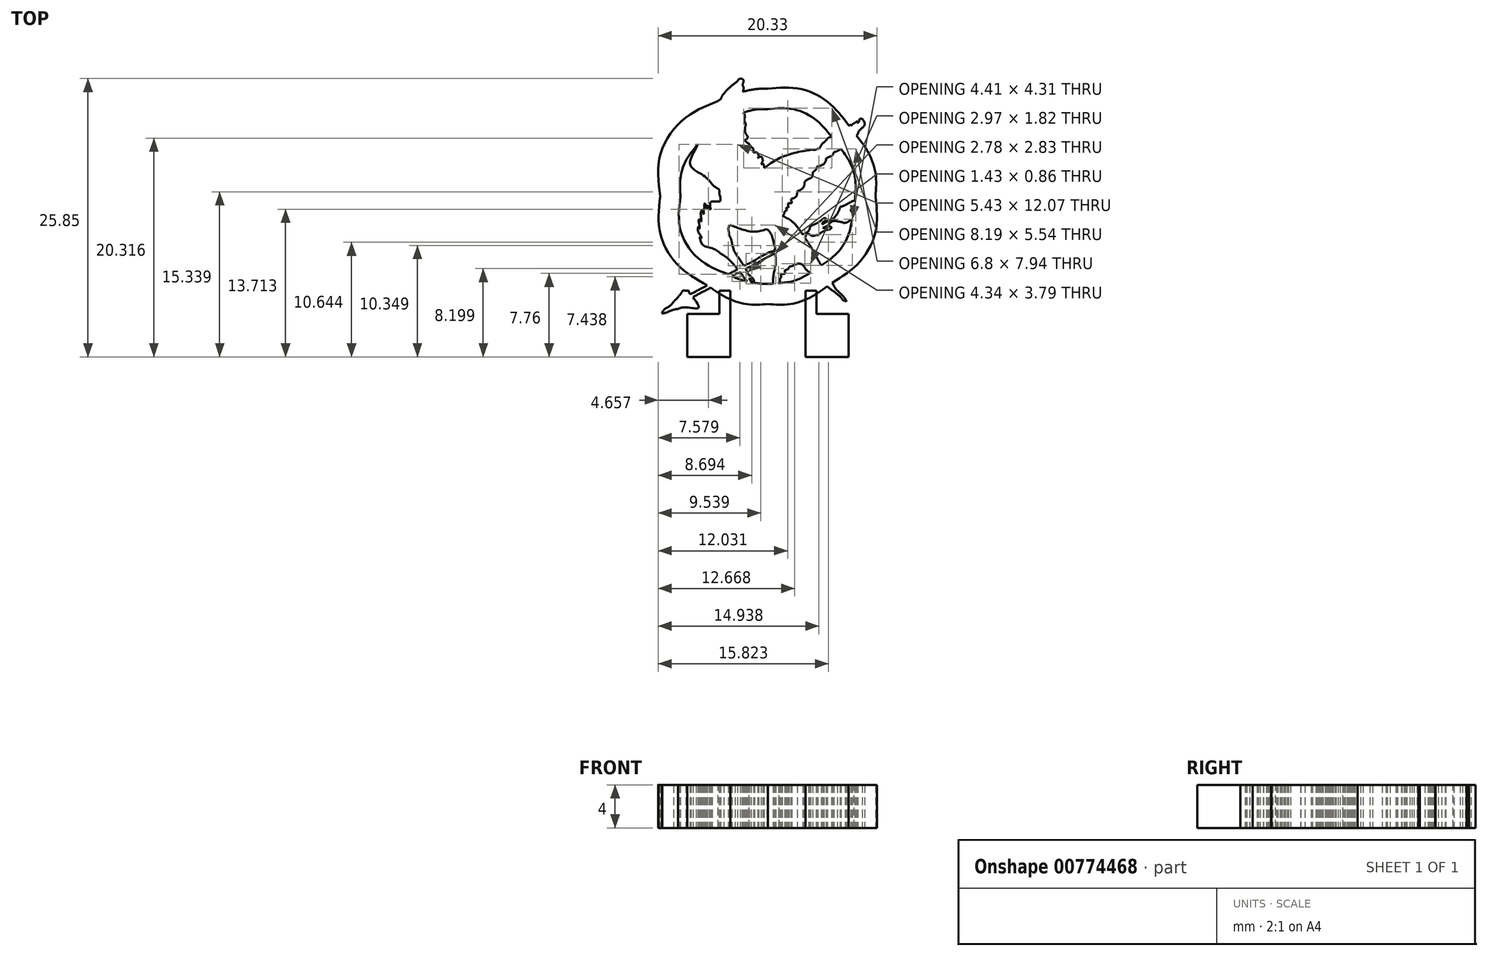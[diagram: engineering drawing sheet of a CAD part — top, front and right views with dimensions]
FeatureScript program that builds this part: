
annotation { "Feature Type Name" : "Feature", "Feature Type Description" : "" }
export const myFeature = defineFeature(function(context is Context, id is Id, definition is map)
    precondition{}
    {
        {
            var Q0;
            Q0=qCreatedBy(makeId("Top.planeOp"),FACE);
            var sketch = newSketch(context, id + "F0", { "sketchPlane" : qUnion([Q0])});
            skFitSpline(sketch, "E0", {"points": [v(6.8, 4.37) * mm, v(7.63, 3.1) * mm, v(8.11, 1.58) * mm, v(8.11, -0.04) * mm]});
            skFitSpline(sketch, "E1", {"points": [v(8.11, -0.04) * mm, v(8.11, -0.15) * mm, v(8.11, -0.27) * mm, v(8.1, -0.38) * mm]});
            skFitSpline(sketch, "E2", {"points": [v(8.08, -0.82) * mm, v(8.06, -1.02) * mm, v(8.03, -1.22) * mm, v(8, -1.41) * mm]});
            skFitSpline(sketch, "E3", {"points": [v(7.84, -2.14) * mm, v(7.37, -3.87) * mm, v(6.35, -5.38) * mm, v(4.97, -6.45) * mm]});
            skFitSpline(sketch, "E4", {"points": [v(5.98, -8.05) * mm, v(8.42, -6.23) * mm, v(10, -3.32) * mm, v(10, -0.04) * mm]});
            skFitSpline(sketch, "E5", {"points": [v(10, -0.04) * mm, v(10, 2.06) * mm, v(9.35, 4) * mm, v(8.24, 5.62) * mm]});
            skFitSpline(sketch, "E6", {"points": [v(3.96, -7.12) * mm, v(3.06, -7.62) * mm, v(2.06, -7.96) * mm, v(1, -8.1) * mm]});
            skFitSpline(sketch, "E7", {"points": [v(0.47, -8.14) * mm, v(0.31, -8.15) * mm, v(0.16, -8.16) * mm, v(0, -8.16) * mm]});
            skFitSpline(sketch, "E8", {"points": [v(0, -8.16) * mm, v(-0.42, -8.16) * mm, v(-0.84, -8.12) * mm, v(-1.25, -8.06) * mm]});
            skFitSpline(sketch, "E9", {"points": [v(-1.32, -8.05) * mm, v(-1.4, -8.03) * mm, v(-1.48, -8.02) * mm, v(-1.56, -8) * mm]});
            skFitSpline(sketch, "E10", {"points": [v(-1.9, -7.93) * mm, v(-2.4, -7.81) * mm, v(-2.87, -7.65) * mm, v(-3.33, -7.44) * mm]});
            skFitSpline(sketch, "E11", {"points": [v(-5.28, -8.5) * mm, v(-5.29, -8.5) * mm, v(-5.3, -8.5) * mm, v(-5.3, -8.51) * mm]});
            skFitSpline(sketch, "E12", {"points": [v(-5.3, -8.51) * mm, v(-3.77, -9.48) * mm, v(-1.95, -10.04) * mm, v(0, -10.04) * mm]});
            skFitSpline(sketch, "E13", {"points": [v(0, -10.04) * mm, v(2.03, -10.04) * mm, v(3.92, -9.43) * mm, v(5.5, -8.39) * mm]});
            skFitSpline(sketch, "E14", {"points": [v(-3.7, -7.26) * mm, v(-6.32, -5.92) * mm, v(-8.11, -3.19) * mm, v(-8.11, -0.04) * mm]});
            skFitSpline(sketch, "E15", {"points": [v(-8.11, -0.04) * mm, v(-8.11, 1.78) * mm, v(-7.51, 3.45) * mm, v(-6.5, 4.8) * mm]});
            skFitSpline(sketch, "E16", {"points": [v(-4.63, 8.82) * mm, v(-7.82, 7.15) * mm, v(-10, 3.8) * mm, v(-10, -0.04) * mm]});
            skFitSpline(sketch, "E17", {"points": [v(-10, -0.04) * mm, v(-10, -3.47) * mm, v(-8.27, -6.5) * mm, v(-5.63, -8.3) * mm]});
            skFitSpline(sketch, "E18", {"points": [v(-2.25, 7.75) * mm, v(-1.54, 7.96) * mm, v(-0.78, 8.07) * mm, v(0, 8.07) * mm]});
            skFitSpline(sketch, "E19", {"points": [v(0, 8.07) * mm, v(2.34, 8.07) * mm, v(4.45, 7.08) * mm, v(5.94, 5.48) * mm]});
            skFitSpline(sketch, "E20", {"points": [v(7.52, 6.54) * mm, v(5.69, 8.63) * mm, v(3, 9.96) * mm, v(0, 9.96) * mm]});
            skFitSpline(sketch, "E21", {"points": [v(0, 9.96) * mm, v(-0.8, 9.96) * mm, v(-1.57, 9.86) * mm, v(-2.31, 9.69) * mm]});
            skFitSpline(sketch, "E22", {"points": [v(-3.62, -3.38) * mm, v(-3.67, -3.09) * mm, v(-3.61, -2.8) * mm, v(-3.43, -2.7) * mm]});
            skFitSpline(sketch, "E23", {"points": [v(-3.43, -2.7) * mm, v(-2.55, -3.05) * mm, v(-1.27, -3.3) * mm, v(-0.1, -3.08) * mm]});
            skFitSpline(sketch, "E24", {"points": [v(-0.1, -3.08) * mm, v(0.21, -3.38) * mm, v(0.4, -3.81) * mm, v(0.54, -4.38) * mm]});
            skFitSpline(sketch, "E25", {"points": [v(0.54, -4.38) * mm, v(0.58, -4.53) * mm, v(0.68, -4.8) * mm, v(0.64, -4.92) * mm]});
            skFitSpline(sketch, "E26", {"points": [v(0.64, -4.92) * mm, v(0.58, -5.08) * mm, v(0.12, -5.22) * mm, v(-0.07, -5.32) * mm]});
            skFitSpline(sketch, "E27", {"points": [v(-0.07, -5.32) * mm, v(-0.77, -5.7) * mm, v(-1.6, -6.18) * mm, v(-2.25, -6.48) * mm]});
            skFitSpline(sketch, "E28", {"points": [v(-2.25, -6.48) * mm, v(-2.6, -5.92) * mm, v(-3.14, -5.07) * mm, v(-3.36, -4.24) * mm]});
            skFitSpline(sketch, "E29", {"points": [v(-3.36, -4.24) * mm, v(-3.44, -3.94) * mm, v(-3.59, -3.63) * mm, v(-3.62, -3.38) * mm]});
            skFitSpline(sketch, "E30", {"points": [v(8, -1.41) * mm, v(7.9, -1.43) * mm, v(7.8, -1.44) * mm, v(7.76, -1.44) * mm]});
            skFitSpline(sketch, "E31", {"points": [v(7.76, -1.44) * mm, v(7.73, -1.41) * mm, v(7.75, -1.33) * mm, v(7.69, -1.33) * mm]});
            skFitSpline(sketch, "E32", {"points": [v(7.69, -1.33) * mm, v(7.79, -1.13) * mm, v(7.93, -0.97) * mm, v(8.08, -0.82) * mm]});
            skFitSpline(sketch, "E33", {"points": [v(8.1, -0.38) * mm, v(7.64, -0.59) * mm, v(7.2, -0.83) * mm, v(6.72, -1.02) * mm]});
            skFitSpline(sketch, "E34", {"points": [v(6.72, -1.02) * mm, v(6.57, -1.41) * mm, v(6.37, -1.75) * mm, v(6.13, -2.06) * mm]});
            skFitSpline(sketch, "E35", {"points": [v(6.13, -2.06) * mm, v(5.76, -2.24) * mm, v(5.4, -2.42) * mm, v(5.06, -2.63) * mm]});
            skFitSpline(sketch, "E36", {"points": [v(5.06, -2.63) * mm, v(5.1, -2.45) * mm, v(5.35, -2.28) * mm, v(5.42, -2.06) * mm]});
            skFitSpline(sketch, "E37", {"points": [v(5.42, -2.06) * mm, v(5.14, -2.1) * mm, v(4.9, -2.31) * mm, v(4.64, -2.46) * mm]});
            skFitSpline(sketch, "E38", {"points": [v(4.64, -2.46) * mm, v(4.38, -2.6) * mm, v(4.1, -2.73) * mm, v(3.88, -2.91) * mm]});
            skFitSpline(sketch, "E39", {"points": [v(3.88, -2.91) * mm, v(3.88, -3.08) * mm, v(3.8, -3.15) * mm, v(3.78, -3.29) * mm]});
            skFitSpline(sketch, "E40", {"points": [v(3.78, -3.29) * mm, v(3.6, -3.39) * mm, v(3.43, -3.49) * mm, v(3.24, -3.57) * mm]});
            skFitSpline(sketch, "E41", {"points": [v(3.24, -3.57) * mm, v(2.74, -2.87) * mm, v(2.13, -2.27) * mm, v(1.35, -1.85) * mm]});
            skFitSpline(sketch, "E42", {"points": [v(1.35, -1.85) * mm, v(1.49, -1.7) * mm, v(1.55, -1.48) * mm, v(1.7, -1.35) * mm]});
            skFitSpline(sketch, "E43", {"points": [v(1.7, -1.35) * mm, v(1.74, -1.3) * mm, v(1.73, -1.2) * mm, v(1.68, -1.18) * mm]});
            skFitSpline(sketch, "E44", {"points": [v(1.68, -1.18) * mm, v(1.73, -1.1) * mm, v(1.85, -1.07) * mm, v(1.92, -1) * mm]});
            skFitSpline(sketch, "E45", {"points": [v(1.92, -1) * mm, v(1.9, -0.67) * mm, v(2.19, -0.65) * mm, v(2.13, -0.28) * mm]});
            skFitSpline(sketch, "E46", {"points": [v(2.13, -0.28) * mm, v(2.45, -0.16) * mm, v(2.67, 0.06) * mm, v(2.72, 0.45) * mm]});
            skFitSpline(sketch, "E47", {"points": [v(2.72, 0.45) * mm, v(3.1, 0.6) * mm, v(3.34, 0.9) * mm, v(3.43, 1.35) * mm]});
            skFitSpline(sketch, "E48", {"points": [v(3.43, 1.35) * mm, v(3.74, 1.57) * mm, v(4.1, 1.76) * mm, v(4.16, 2.23) * mm]});
            skFitSpline(sketch, "E49", {"points": [v(4.16, 2.23) * mm, v(4.35, 2.34) * mm, v(4.49, 2.5) * mm, v(4.56, 2.72) * mm]});
            skFitSpline(sketch, "E50", {"points": [v(4.56, 2.72) * mm, v(4.97, 2.86) * mm, v(5.3, 3.08) * mm, v(5.42, 3.5) * mm]});
            skFitSpline(sketch, "E51", {"points": [v(5.42, 3.5) * mm, v(5.71, 3.64) * mm, v(5.99, 3.79) * mm, v(6.13, 4.07) * mm]});
            skFitSpline(sketch, "E52", {"points": [v(6.13, 4.07) * mm, v(6.3, 4.13) * mm, v(6.58, 4.26) * mm, v(6.8, 4.37) * mm]});
            skFitSpline(sketch, "E53", {"points": [v(8.33, 5.73) * mm, v(8.55, 6.15) * mm, v(8.98, 6.6) * mm, v(8.78, 7.17) * mm]});
            skFitSpline(sketch, "E54", {"points": [v(8.78, 7.17) * mm, v(8.53, 7.15) * mm, v(8.47, 6.94) * mm, v(8.35, 6.8) * mm]});
            skFitSpline(sketch, "E55", {"points": [v(8.35, 6.8) * mm, v(8.3, 6.83) * mm, v(8.3, 6.92) * mm, v(8.19, 6.89) * mm]});
            skFitSpline(sketch, "E56", {"points": [v(8.19, 6.89) * mm, v(8.02, 6.77) * mm, v(7.85, 6.65) * mm, v(7.71, 6.5) * mm]});
            skFitSpline(sketch, "E57", {"points": [v(7.71, 6.5) * mm, v(7.7, 6.61) * mm, v(7.57, 6.56) * mm, v(7.52, 6.54) * mm]});
            skLineSegment(sketch, "E58", {"start": v(8.24, 5.62) * mm, "end": v(8.33, 5.73) * mm});
            skFitSpline(sketch, "E59", {"points": [v(5.94, 5.48) * mm, v(5.63, 5.42) * mm, v(5.43, 5.2) * mm, v(5.2, 5) * mm]});
            skFitSpline(sketch, "E60", {"points": [v(5.2, 5) * mm, v(5, 4.8) * mm, v(4.8, 4.48) * mm, v(4.56, 4.38) * mm]});
            skFitSpline(sketch, "E61", {"points": [v(4.56, 4.38) * mm, v(4.38, 4.3) * mm, v(4.08, 4.3) * mm, v(3.83, 4.26) * mm]});
            skFitSpline(sketch, "E62", {"points": [v(3.83, 4.26) * mm, v(2.27, 3.96) * mm, v(0.79, 3.37) * mm, v(-0.33, 2.6) * mm]});
            skFitSpline(sketch, "E63", {"points": [v(-0.33, 2.6) * mm, v(-0.36, 2.8) * mm, v(-0.41, 2.96) * mm, v(-0.64, 2.96) * mm]});
            skFitSpline(sketch, "E64", {"points": [v(-0.64, 2.96) * mm, v(-0.5, 3.21) * mm, v(-0.6, 3.65) * mm, v(-0.95, 3.53) * mm]});
            skFitSpline(sketch, "E65", {"points": [v(-0.95, 3.53) * mm, v(-0.87, 3.8) * mm, v(-1.1, 4.07) * mm, v(-1.33, 4.02) * mm]});
            skFitSpline(sketch, "E66", {"points": [v(-1.33, 4.02) * mm, v(-1.34, 4.3) * mm, v(-1.45, 4.5) * mm, v(-1.8, 4.45) * mm]});
            skFitSpline(sketch, "E67", {"points": [v(-1.8, 4.45) * mm, v(-1.71, 4.8) * mm, v(-1.97, 5) * mm, v(-2.13, 5.18) * mm]});
            skFitSpline(sketch, "E68", {"points": [v(-2.13, 5.18) * mm, v(-1.87, 5.47) * mm, v(-2.07, 5.84) * mm, v(-2.1, 6.2) * mm]});
            skFitSpline(sketch, "E69", {"points": [v(-2.1, 6.2) * mm, v(-2.13, 6.38) * mm, v(-2.06, 6.56) * mm, v(-2.09, 6.74) * mm]});
            skFitSpline(sketch, "E70", {"points": [v(-2.09, 6.74) * mm, v(-2.1, 6.83) * mm, v(-2.17, 6.92) * mm, v(-2.18, 7) * mm]});
            skFitSpline(sketch, "E71", {"points": [v(-2.18, 7) * mm, v(-2.2, 7.15) * mm, v(-2.14, 7.31) * mm, v(-2.16, 7.45) * mm]});
            skFitSpline(sketch, "E72", {"points": [v(-2.16, 7.45) * mm, v(-2.17, 7.58) * mm, v(-2.24, 7.66) * mm, v(-2.25, 7.75) * mm]});
            skFitSpline(sketch, "E73", {"points": [v(-2.3, 9.75) * mm, v(-2.26, 9.96) * mm, v(-2.27, 10.15) * mm, v(-2.37, 10.3) * mm]});
            skFitSpline(sketch, "E74", {"points": [v(-2.37, 10.3) * mm, v(-2.3, 10.5) * mm, v(-2.27, 10.77) * mm, v(-2.42, 10.9) * mm]});
            skFitSpline(sketch, "E75", {"points": [v(-2.42, 10.9) * mm, v(-2.68, 10.87) * mm, v(-2.84, 10.66) * mm, v(-3.03, 10.5) * mm]});
            skFitSpline(sketch, "E76", {"points": [v(-3.03, 10.5) * mm, v(-3.42, 10.2) * mm, v(-3.78, 9.86) * mm, v(-4.1, 9.5) * mm]});
            skFitSpline(sketch, "E77", {"points": [v(-4.1, 9.5) * mm, v(-4.25, 9.3) * mm, v(-4.37, 9.04) * mm, v(-4.55, 8.9) * mm]});
            skFitSpline(sketch, "E78", {"points": [v(-4.55, 8.9) * mm, v(-4.58, 8.87) * mm, v(-4.6, 8.85) * mm, v(-4.63, 8.82) * mm]});
            skFitSpline(sketch, "E79", {"points": [v(-6.5, 4.8) * mm, v(-6.55, 4.68) * mm, v(-6.64, 4.54) * mm, v(-6.67, 4.42) * mm]});
            skFitSpline(sketch, "E80", {"points": [v(-6.67, 4.42) * mm, v(-7.2, 2.85) * mm, v(-5.96, 1.89) * mm, v(-5.16, 1.1) * mm]});
            skFitSpline(sketch, "E81", {"points": [v(-5.16, 1.1) * mm, v(-4.92, 0.84) * mm, v(-4.54, 0.6) * mm, v(-4.52, 0.24) * mm]});
            skFitSpline(sketch, "E82", {"points": [v(-4.52, 0.24) * mm, v(-4.48, -0.48) * mm, v(-5.27, -0.53) * mm, v(-5.3, -1.25) * mm]});
            skFitSpline(sketch, "E83", {"points": [v(-5.3, -1.25) * mm, v(-5.44, -1.17) * mm, v(-5.45, -0.98) * mm, v(-5.61, -0.92) * mm]});
            skFitSpline(sketch, "E84", {"points": [v(-5.61, -0.92) * mm, v(-5.7, -0.94) * mm, v(-5.6, -1.07) * mm, v(-5.64, -1.18) * mm]});
            skFitSpline(sketch, "E85", {"points": [v(-5.64, -1.18) * mm, v(-5.75, -1.04) * mm, v(-5.77, -0.8) * mm, v(-5.92, -0.69) * mm]});
            skFitSpline(sketch, "E86", {"points": [v(-5.92, -0.69) * mm, v(-5.9, -1.03) * mm, v(-5.96, -1.3) * mm, v(-5.94, -1.66) * mm]});
            skFitSpline(sketch, "E87", {"points": [v(-5.94, -1.66) * mm, v(-6.05, -1.6) * mm, v(-6, -1.38) * mm, v(-6.06, -1.28) * mm]});
            skFitSpline(sketch, "E88", {"points": [v(-6.06, -1.28) * mm, v(-6.22, -1.5) * mm, v(-6.2, -2.01) * mm, v(-6.18, -2.34) * mm]});
            skFitSpline(sketch, "E89", {"points": [v(-6.18, -2.34) * mm, v(-6.2, -2.38) * mm, v(-6.23, -2.2) * mm, v(-6.23, -2.13) * mm]});
            skFitSpline(sketch, "E90", {"points": [v(-6.23, -2.13) * mm, v(-6.43, -2.24) * mm, v(-6.36, -2.65) * mm, v(-6.34, -2.91) * mm]});
            skFitSpline(sketch, "E91", {"points": [v(-6.34, -2.91) * mm, v(-6.36, -3.03) * mm, v(-6.42, -2.83) * mm, v(-6.46, -2.82) * mm]});
            skFitSpline(sketch, "E92", {"points": [v(-6.46, -2.82) * mm, v(-6.48, -3.3) * mm, v(-6.3, -3.6) * mm, v(-6.13, -3.9) * mm]});
            skFitSpline(sketch, "E93", {"points": [v(-6.13, -3.9) * mm, v(-6.2, -3.88) * mm, v(-6.24, -3.81) * mm, v(-6.32, -3.79) * mm]});
            skFitSpline(sketch, "E94", {"points": [v(-6.32, -3.79) * mm, v(-6, -4.58) * mm, v(-5.09, -4.88) * mm, v(-4.38, -5.35) * mm]});
            skFitSpline(sketch, "E95", {"points": [v(-4.38, -5.35) * mm, v(-3.75, -5.76) * mm, v(-3.27, -6.25) * mm, v(-2.82, -6.8) * mm]});
            skFitSpline(sketch, "E96", {"points": [v(-2.82, -6.8) * mm, v(-3.1, -6.96) * mm, v(-3.4, -7.11) * mm, v(-3.7, -7.26) * mm]});
            skLineSegment(sketch, "E97", {"start": v(-2.31, 9.69) * mm, "end": v(-2.3, 9.75) * mm});
            skFitSpline(sketch, "E98", {"points": [v(-5.63, -8.3) * mm, v(-6, -8.49) * mm, v(-6.75, -8.88) * mm, v(-7.13, -9.09) * mm]});
            skFitSpline(sketch, "E99", {"points": [v(-7.13, -9.09) * mm, v(-7.3, -9.02) * mm, v(-7.34, -8.8) * mm, v(-7.62, -8.8) * mm]});
            skFitSpline(sketch, "E100", {"points": [v(-7.62, -8.8) * mm, v(-7.9, -8.8) * mm, v(-8.05, -9.03) * mm, v(-8.24, -9.25) * mm]});
            skFitSpline(sketch, "E101", {"points": [v(-8.24, -9.25) * mm, v(-8.41, -9.47) * mm, v(-8.61, -9.67) * mm, v(-8.76, -9.82) * mm]});
            skFitSpline(sketch, "E102", {"points": [v(-8.76, -9.82) * mm, v(-9.17, -10.26) * mm, v(-9.6, -10.52) * mm, v(-9.85, -10.9) * mm]});
            skFitSpline(sketch, "E103", {"points": [v(-9.85, -10.9) * mm, v(-9.84, -10.9) * mm, v(-9.83, -10.9) * mm, v(-9.82, -10.9) * mm]});
            skFitSpline(sketch, "E104", {"points": [v(-9.82, -10.9) * mm, v(-9.4, -10.8) * mm, v(-8.94, -10.62) * mm, v(-8.33, -10.48) * mm]});
            skFitSpline(sketch, "E105", {"points": [v(-8.33, -10.48) * mm, v(-7.64, -10.33) * mm, v(-6.45, -10.38) * mm, v(-6.96, -9.4) * mm]});
            skFitSpline(sketch, "E106", {"points": [v(-6.96, -9.4) * mm, v(-6.42, -9.1) * mm, v(-5.86, -8.8) * mm, v(-5.3, -8.51) * mm]});
            skFitSpline(sketch, "E107", {"points": [v(-3.33, -7.44) * mm, v(-3.08, -7.31) * mm, v(-2.76, -7.15) * mm, v(-2.58, -7.07) * mm]});
            skFitSpline(sketch, "E108", {"points": [v(-2.58, -7.07) * mm, v(-2.35, -7.36) * mm, v(-2.16, -7.68) * mm, v(-1.9, -7.93) * mm]});
            skFitSpline(sketch, "E109", {"points": [v(-1.56, -8) * mm, v(-1.62, -7.89) * mm, v(-1.68, -7.77) * mm, v(-1.75, -7.67) * mm]});
            skFitSpline(sketch, "E110", {"points": [v(-1.75, -7.67) * mm, v(-1.61, -7.72) * mm, v(-1.5, -7.93) * mm, v(-1.32, -8.05) * mm]});
            skFitSpline(sketch, "E111", {"points": [v(-1.25, -8.06) * mm, v(-1.46, -7.57) * mm, v(-1.84, -7.24) * mm, v(-2.04, -6.74) * mm]});
            skFitSpline(sketch, "E112", {"points": [v(-2.04, -6.74) * mm, v(-1.1, -6.3) * mm, v(-0.25, -5.77) * mm, v(0.69, -5.32) * mm]});
            skFitSpline(sketch, "E113", {"points": [v(0.69, -5.32) * mm, v(0.72, -6.37) * mm, v(0.55, -7.2) * mm, v(0.47, -8.14) * mm]});
            skFitSpline(sketch, "E114", {"points": [v(1, -8.1) * mm, v(1.01, -8.06) * mm, v(1.03, -8.04) * mm, v(1.04, -8.02) * mm]});
            skFitSpline(sketch, "E115", {"points": [v(1.04, -8.02) * mm, v(1.13, -7.88) * mm, v(1.13, -7.67) * mm, v(1.25, -7.57) * mm]});
            skFitSpline(sketch, "E116", {"points": [v(1.25, -7.57) * mm, v(1.24, -7.24) * mm, v(1.54, -7.22) * mm, v(1.56, -6.9) * mm]});
            skFitSpline(sketch, "E117", {"points": [v(1.56, -6.9) * mm, v(1.74, -6.84) * mm, v(1.9, -6.76) * mm, v(1.96, -6.58) * mm]});
            skFitSpline(sketch, "E118", {"points": [v(1.96, -6.58) * mm, v(2.4, -6.43) * mm, v(2.85, -6.26) * mm, v(3.31, -6.46) * mm]});
            skFitSpline(sketch, "E119", {"points": [v(3.31, -6.46) * mm, v(3.47, -6.73) * mm, v(3.68, -6.96) * mm, v(3.96, -7.12) * mm]});
            skFitSpline(sketch, "E120", {"points": [v(5.54, -8.43) * mm, v(5.82, -8.66) * mm, v(6.14, -8.87) * mm, v(6.44, -9.1) * mm]});
            skFitSpline(sketch, "E121", {"points": [v(6.44, -9.1) * mm, v(6.73, -9.35) * mm, v(6.98, -9.66) * mm, v(7.3, -9.8) * mm]});
            skFitSpline(sketch, "E122", {"points": [v(7.3, -9.8) * mm, v(6.95, -9.25) * mm, v(6.38, -8.7) * mm, v(6, -8.1) * mm]});
            skLineSegment(sketch, "E123", {"start": v(6, -8.1) * mm, "end": v(5.98, -8.05) * mm});
            skFitSpline(sketch, "E124", {"points": [v(4.97, -6.45) * mm, v(4.46, -5.58) * mm, v(3.97, -4.7) * mm, v(3.43, -3.86) * mm]});
            skFitSpline(sketch, "E125", {"points": [v(3.43, -3.86) * mm, v(3.7, -3.52) * mm, v(4.07, -3.68) * mm, v(4.5, -3.62) * mm]});
            skFitSpline(sketch, "E126", {"points": [v(4.5, -3.62) * mm, v(4.72, -3.58) * mm, v(4.97, -3.38) * mm, v(5.2, -3.26) * mm]});
            skFitSpline(sketch, "E127", {"points": [v(5.2, -3.26) * mm, v(5.47, -3.14) * mm, v(5.75, -3.1) * mm, v(5.91, -2.91) * mm]});
            skFitSpline(sketch, "E128", {"points": [v(5.91, -2.91) * mm, v(5.71, -2.81) * mm, v(5.38, -2.97) * mm, v(5.11, -2.96) * mm]});
            skFitSpline(sketch, "E129", {"points": [v(5.11, -2.96) * mm, v(5.6, -2.7) * mm, v(5.94, -2.36) * mm, v(6.77, -2.41) * mm]});
            skFitSpline(sketch, "E130", {"points": [v(6.77, -2.41) * mm, v(6.9, -2.42) * mm, v(7.04, -2.5) * mm, v(7.17, -2.48) * mm]});
            skFitSpline(sketch, "E131", {"points": [v(7.17, -2.48) * mm, v(7.28, -2.47) * mm, v(7.57, -2.3) * mm, v(7.84, -2.14) * mm]});
            skLineSegment(sketch, "E132", {"start": v(5.5, -8.39) * mm, "end": v(5.54, -8.43) * mm});
            skSolve(sketch);
        }
        {
            var Q0;
            Q0=qCreatedBy(makeId("Top.planeOp"),FACE);
            var sketch = newSketch(context, id + "F1", { "sketchPlane" : qUnion([Q0])});
            skLineSegment(sketch, "E133.bottom", {"start": v(-7.5, -10.94) * mm, "end": v(-3.5, -10.94) * mm});
            skLineSegment(sketch, "E133.top", {"start": v(-7.5, -14.94) * mm, "end": v(-3.5, -14.94) * mm});
            skLineSegment(sketch, "E133.left", {"start": v(-7.5, -10.94) * mm, "end": v(-7.5, -14.94) * mm});
            skLineSegment(sketch, "E133.right", {"start": v(-3.5, -10.94) * mm, "end": v(-3.5, -14.94) * mm});
            skLineSegment(sketch, "E134.MirrorCS", {"start": v(7.5, -14.94) * mm, "end": v(3.5, -14.94) * mm});
            skLineSegment(sketch, "E135.MirrorCS", {"start": v(3.5, -10.94) * mm, "end": v(3.5, -14.94) * mm});
            skLineSegment(sketch, "E136.MirrorCS", {"start": v(7.5, -10.94) * mm, "end": v(3.5, -10.94) * mm});
            skLineSegment(sketch, "E137.MirrorCS", {"start": v(7.5, -10.94) * mm, "end": v(7.5, -14.94) * mm});
            skLineSegment(sketch, "E138", {"start": v(-9.83, -10.94) * mm, "end": v(-3.51, -10.94) * mm, "construction": true});
            skLineSegment(sketch, "E139.bottom", {"start": v(-3.5, -11.25) * mm, "end": v(-4.5, -11.25) * mm});
            skLineSegment(sketch, "E139.top", {"start": v(-3.5, -8.78) * mm, "end": v(-4.5, -8.78) * mm});
            skLineSegment(sketch, "E139.left", {"start": v(-3.5, -11.25) * mm, "end": v(-3.5, -8.78) * mm});
            skLineSegment(sketch, "E139.right", {"start": v(-4.5, -11.25) * mm, "end": v(-4.5, -8.78) * mm});
            skLineSegment(sketch, "E140.MirrorCS", {"start": v(3.5, -11.25) * mm, "end": v(3.5, -8.78) * mm});
            skLineSegment(sketch, "E141.MirrorCS", {"start": v(3.5, -11.25) * mm, "end": v(4.5, -11.25) * mm});
            skLineSegment(sketch, "E142.MirrorCS", {"start": v(4.5, -11.25) * mm, "end": v(4.5, -8.78) * mm});
            skLineSegment(sketch, "E143.MirrorCS", {"start": v(3.5, -8.78) * mm, "end": v(4.5, -8.78) * mm});
            skSolve(sketch);
        }
        {
            var Q0;
            Q0=makeQuery(id+"F0.imprint","IMPRINT",FACE,{"disambiguationData":[TD([[makeQuery(id+"F0.imprint","IMPRINT",EDGE,{"derivedFrom":sQuery(id+"F0.wireOp",EDGE,"E0")}),1.0]])]});
            var Q1;
            Q1 = qSketchRegion(id + "F1", true);
            extrude(context, id + "F2", {"entities" : qUnion([Q0, Q1]), "endBound" : BoundingType.SYMMETRIC, "depth" : 4 * mm, "offsetDistance" : 25 * mm});
        }
    });
